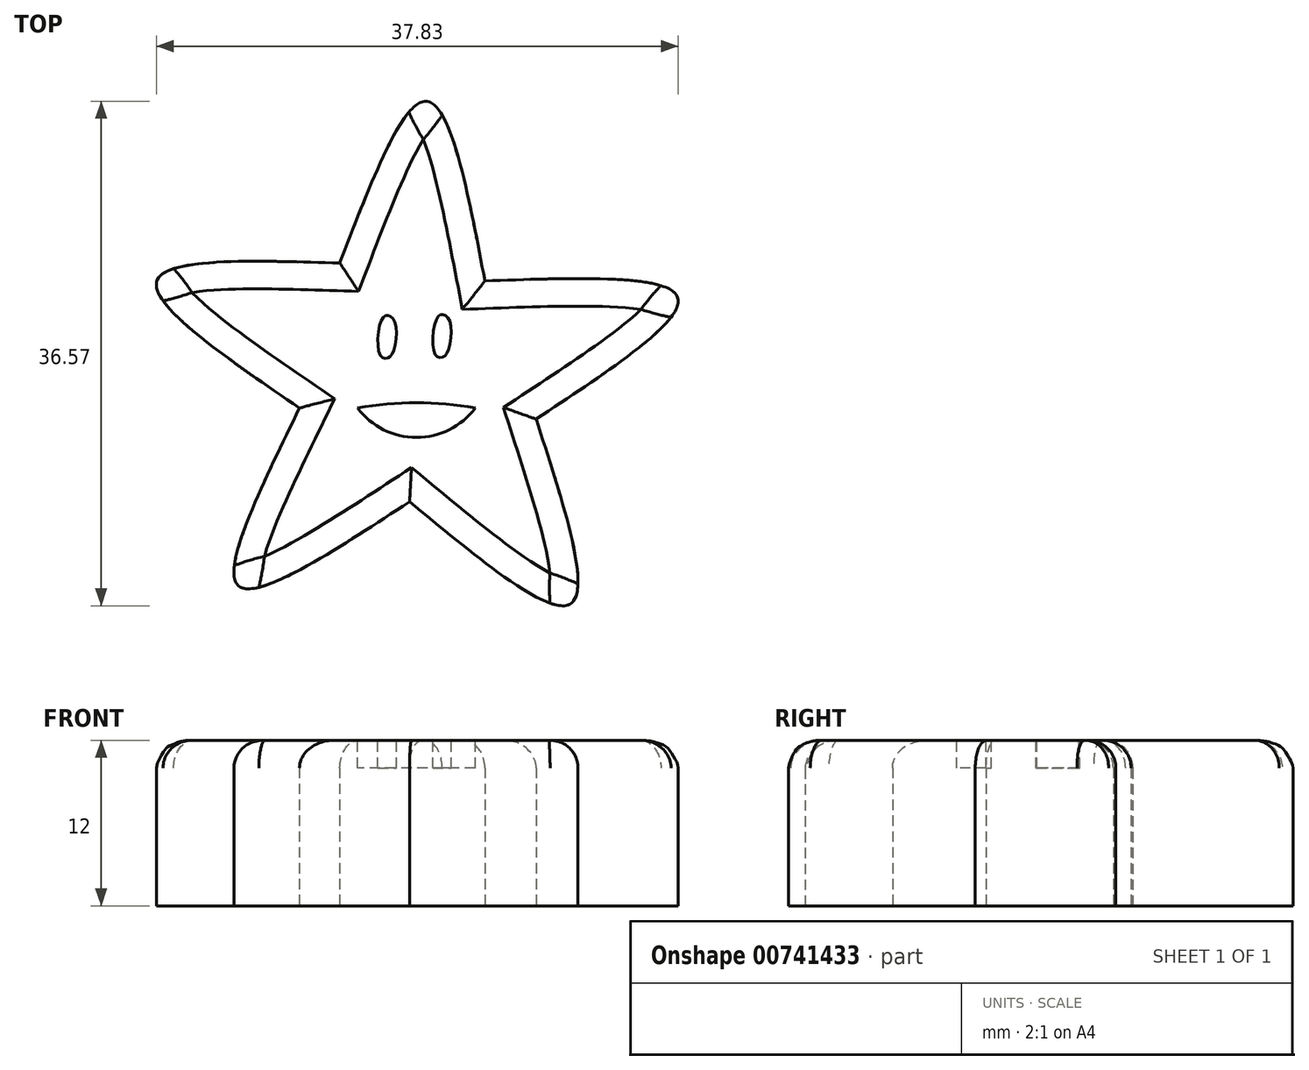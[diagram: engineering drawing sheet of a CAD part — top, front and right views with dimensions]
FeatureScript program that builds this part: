
annotation { "Feature Type Name" : "Feature", "Feature Type Description" : "" }
export const myFeature = defineFeature(function(context is Context, id is Id, definition is map)
    precondition{}
    {
        {
            var Q0;
            Q0=qCreatedBy(makeId("Top.planeOp"),FACE);
            var sketch = newSketch(context, id + "F0", { "sketchPlane" : qUnion([Q0])});
            skLineSegment(sketch, "E0.bottom", {"start": v(25, -20.84) * mm, "end": v(-25, -20.84) * mm});
            skLineSegment(sketch, "E0.top", {"start": v(25, 29.16) * mm, "end": v(-25, 29.16) * mm});
            skLineSegment(sketch, "E0.left", {"start": v(25, -20.84) * mm, "end": v(25, 29.16) * mm});
            skLineSegment(sketch, "E0.right", {"start": v(-25, -20.84) * mm, "end": v(-25, 29.16) * mm});
            skPoint(sketch, "E0.middle", {"position": v(0, 4.16) * mm});
            skSolve(sketch);
        }
        {
            var Q0;
            Q0=qCreatedBy(makeId("Top.planeOp"),FACE);
            var sketch = newSketch(context, id + "F1", { "sketchPlane" : qUnion([Q0])});
            skFitSpline(sketch, "E1", {"points": [v(-5.06, 10.5) * mm, v(1.24, 22.23) * mm, v(5.46, 9.21) * mm], "startDerivative": vector(13.75, 35.91) * mm, "endDerivative": vector(7.31, -38.33) * mm});
            skFitSpline(sketch, "E2", {"points": [v(5.46, 9.21) * mm, v(19.44, 8) * mm, v(9.17, -0.8) * mm], "startDerivative": vector(39.9, 1.48) * mm, "endDerivative": vector(-32.7, -21.56) * mm});
            skFitSpline(sketch, "E3", {"points": [v(9.17, -0.8) * mm, v(11.68, -14.18) * mm, v(0, -6.8) * mm], "startDerivative": vector(12.08, -37.22) * mm, "endDerivative": vector(-30.37, 25.15) * mm});
            skFitSpline(sketch, "E4", {"points": [v(-5.06, 10.5) * mm, v(-18.32, 9.21) * mm, v(-7.98, 0) * mm], "startDerivative": vector(-38.48, 1.26) * mm, "endDerivative": vector(32.4, -22.2) * mm});
            skFitSpline(sketch, "E5", {"points": [v(-7.98, 0) * mm, v(-12.41, -12.88) * mm, v(0, -6.8) * mm], "startDerivative": vector(-17.27, -35.33) * mm, "endDerivative": vector(33.18, 21.68) * mm});
            skSolve(sketch);
        }
        {
            var Q0;
            Q0=qSketchRegion(id+"F1",true);
            extrude(context, id + "F2", {"entities" : qUnion([Q0]), "depth" : 12 * mm, "offsetDistance" : 25 * mm});
        }
        {
            var Q0;
            Q0=makeQuery(id+"F2.opExtrude","CAP_EDGE",EDGE,{"disambiguationData":[OSD([sQuery(id+"F1.wireOp",EDGE,"E4")])],"isStart":false});
            var Q1;
            Q1=makeQuery(id+"F2.opExtrude","CAP_EDGE",EDGE,{"disambiguationData":[OSD([sQuery(id+"F1.wireOp",EDGE,"E5")])],"isStart":false});
            var Q2;
            Q2=makeQuery(id+"F2.opExtrude","CAP_EDGE",EDGE,{"disambiguationData":[OSD([sQuery(id+"F1.wireOp",EDGE,"E3")])],"isStart":false});
            var Q3;
            Q3=makeQuery(id+"F2.opExtrude","CAP_EDGE",EDGE,{"disambiguationData":[OSD([sQuery(id+"F1.wireOp",EDGE,"E2")])],"isStart":false});
            var Q4;
            Q4=makeQuery(id+"F2.opExtrude","CAP_EDGE",EDGE,{"disambiguationData":[OSD([sQuery(id+"F1.wireOp",EDGE,"E1")])],"isStart":false});
            fillet(context, id + "F3", {"entities" : qUnion([Q0, Q1, Q2, Q3, Q4]), "radius" : 2 * mm, "tangentPropagation" : true, "allowEdgeOverflow" : false});
        }
        {
            var Q0;
            Q0=makeQuery(id+"F2.opExtrude","CAP_FACE",FACE,{"disambiguationData":[OSD([sQuery(id+"F1.wireOp",EDGE,"ea22f027-b894-4d35-ad94-6574a105fb3a"),sQuery(id+"F1.wireOp",EDGE,"02972ecb-89ef-400d-9b9c-b38da18b9f26"),sQuery(id+"F1.wireOp",EDGE,"d4665c4b-3644-410e-b7a9-793b46f9e3d8"),sQuery(id+"F1.wireOp",EDGE,"4904a858-6bfa-4176-8c43-c28e2eb22261"),sQuery(id+"F1.wireOp",EDGE,"281288f6-0dfc-4ab6-aa52-0887e6a29920"),sQuery(id+"F1.wireOp",EDGE,"e6a59349-29be-4dfa-85ae-5f5bb5e19001"),sQuery(id+"F1.wireOp",EDGE,"33865bf9-fee0-4887-a290-a33334908563"),sQuery(id+"F1.wireOp",EDGE,"b5a1ea3e-0a3a-46d1-a9d2-b11f3d4d393f"),sQuery(id+"F1.wireOp",EDGE,"9160b71b-1dbf-454e-b8aa-38d11ad0787a"),sQuery(id+"F1.wireOp",EDGE,"508b1097-dadd-43a8-a367-845bdcffccfe"),sQuery(id+"F1.wireOp",EDGE,"49bc861f-a654-40ca-8a3d-e641ddbf638b"),sQuery(id+"F1.wireOp",EDGE,"b91fa5d4-4bf4-43ae-99f3-f47139d4a982"),sQuery(id+"F1.wireOp",EDGE,"91c30a01-8c2e-4a9e-bc94-6af126d221bb"),sQuery(id+"F1.wireOp",EDGE,"46226220-93ab-4b08-822d-1d4fcd13f7f0"),sQuery(id+"F1.wireOp",EDGE,"3cccdf76-d96c-4aba-a423-c60eeaef6f2e"),sQuery(id+"F1.wireOp",EDGE,"a7a83c28-3530-49f8-9c53-c2483f9e7872"),sQuery(id+"F1.wireOp",EDGE,"bd418752-b331-4a27-85c2-437b8f3f9da8"),sQuery(id+"F1.wireOp",EDGE,"d86c6e9c-a8e8-46bc-9cbd-8a8ccbf43cd8"),sQuery(id+"F1.wireOp",EDGE,"18ce2d2a-cbe7-4d55-9af2-434ca90d4d8a"),sQuery(id+"F1.wireOp",EDGE,"3e9cf44d-97a5-4047-a5a6-f93e2a769566"),sQuery(id+"F1.wireOp",EDGE,"72104b77-425f-43ce-bfee-662c898d3039"),sQuery(id+"F1.wireOp",EDGE,"b0c94266-c951-4a47-ba1d-05842cc99b57"),sQuery(id+"F1.wireOp",EDGE,"a3bab185-7591-47d8-8c31-848ac42d466f"),sQuery(id+"F1.wireOp",EDGE,"95482d24-3030-4f51-9019-3cd7c5544abc"),sQuery(id+"F1.wireOp",EDGE,"ecb43bb9-7518-4037-82ed-3b3d48b88220"),sQuery(id+"F1.wireOp",EDGE,"6709acc4-015e-4cee-b4b1-e8162d60af49"),sQuery(id+"F1.wireOp",EDGE,"9c087dd5-8d5f-4c13-9bc7-0dec2b4ae27f"),sQuery(id+"F1.wireOp",EDGE,"1f7cd400-eb1a-477a-a8e0-1a1905c8875b"),sQuery(id+"F1.wireOp",EDGE,"2f4714a1-4b7a-4e27-a0f3-d2b64ee53851"),sQuery(id+"F1.wireOp",EDGE,"cf6d8417-590a-48c5-99af-b32b253a895c"),sQuery(id+"F1.wireOp",EDGE,"93dc3e3c-f9e4-4bb0-b6ea-1e3b1bb8eda1"),sQuery(id+"F1.wireOp",EDGE,"f410118d-9d75-4c7b-a8da-20c13fada343"),sQuery(id+"F1.wireOp",EDGE,"eae4d265-d466-4ba0-ad54-7133bb8090aa"),sQuery(id+"F1.wireOp",EDGE,"29f3a1ae-a44a-4252-90b8-49e4f717a763"),sQuery(id+"F1.wireOp",EDGE,"d95e87fc-c752-4cd3-ba2f-4e1b622d11e6"),sQuery(id+"F1.wireOp",EDGE,"42a256c7-bd9f-4b82-a40e-3aa7b43a7311"),sQuery(id+"F1.wireOp",EDGE,"5cccd7cb-d227-495f-bd2e-dd321fa3711f"),sQuery(id+"F1.wireOp",EDGE,"4779d78b-67a4-4074-8e1d-094c3c882748"),sQuery(id+"F1.wireOp",EDGE,"d78c889f-446d-499c-940c-2d769212d2d6"),sQuery(id+"F1.wireOp",EDGE,"5978d452-f883-4c3a-89cf-e77a3d4812d3"),sQuery(id+"F1.wireOp",EDGE,"d596c75f-4af1-4a7b-b4a9-307fc33695f2"),sQuery(id+"F1.wireOp",EDGE,"ac6da6d2-c422-4b3f-ab3b-024f16e2174f"),sQuery(id+"F1.wireOp",EDGE,"f701fbac-f9f2-41ce-b398-1cdb972a07c6"),sQuery(id+"F1.wireOp",EDGE,"6ea0370e-b9df-47c8-82b6-4bf531107383"),sQuery(id+"F1.wireOp",EDGE,"93d4d691-acf9-4093-813e-c243a6abfd77"),sQuery(id+"F1.wireOp",EDGE,"564c231c-7281-4956-8916-2b9847646294"),sQuery(id+"F1.wireOp",EDGE,"447afba2-fe07-4bf1-a098-a2fa503544db"),sQuery(id+"F1.wireOp",EDGE,"783018d8-4da7-439e-baff-4ea1af6aeaae"),sQuery(id+"F1.wireOp",EDGE,"23360fc8-9112-4eab-be8c-d36215a4c504"),sQuery(id+"F1.wireOp",EDGE,"f39823fe-76bf-4b28-8de3-5866c156ca6e"),sQuery(id+"F1.wireOp",EDGE,"94261188-8fe8-4fe3-9cfb-41c0c768c078"),sQuery(id+"F1.wireOp",EDGE,"639eefb3-3c81-4241-8da9-6294a00eecad"),sQuery(id+"F1.wireOp",EDGE,"63a26b51-3e8c-4d7f-a8c5-c852ed6635fd"),sQuery(id+"F1.wireOp",EDGE,"0cbcce5a-d863-44dc-85fc-889f0cb27286"),sQuery(id+"F1.wireOp",EDGE,"41481716-7baf-47e6-bab9-346e36ad7ed7"),sQuery(id+"F1.wireOp",EDGE,"a0ece215-4608-46fb-b9de-0966884f3722"),sQuery(id+"F1.wireOp",EDGE,"cea85d6a-f16e-43e1-82ab-1eb20eedc667"),sQuery(id+"F1.wireOp",EDGE,"90b3652e-c92f-4129-b232-5fc3862136ad"),sQuery(id+"F1.wireOp",EDGE,"d85ff010-6106-4afe-aa78-55669356d399"),sQuery(id+"F1.wireOp",EDGE,"7b3810e8-a3aa-46c5-9845-10c95717e511"),sQuery(id+"F1.wireOp",EDGE,"32d08b1a-e728-49a8-914d-c4ecc0554df0"),sQuery(id+"F1.wireOp",EDGE,"a932f2cb-edb6-4d43-8a31-36080f450e31"),sQuery(id+"F1.wireOp",EDGE,"6d77b220-5459-4ded-ba71-0805bf8e97fe"),sQuery(id+"F1.wireOp",EDGE,"d4a3d79f-eb9b-45d3-af4d-7f6e0c1d0b6a"),sQuery(id+"F1.wireOp",EDGE,"3a8167d0-93d4-4fee-93fc-e765f78cc71a"),sQuery(id+"F1.wireOp",EDGE,"275b4ef8-3749-467f-b8de-4c5ca6efd012"),sQuery(id+"F1.wireOp",EDGE,"250f3aee-73fb-4a09-89d3-a25958f34bab"),sQuery(id+"F1.wireOp",EDGE,"6f7494f2-175a-490b-9ca9-9ab7524c1492"),sQuery(id+"F1.wireOp",EDGE,"d4bde236-d2fc-4dbc-ba9a-6cd55d3f6a15"),sQuery(id+"F1.wireOp",EDGE,"989c9d0c-4ceb-449c-bc73-c96cc92b2f1a"),sQuery(id+"F1.wireOp",EDGE,"78fda69b-8c10-4e3c-872b-102a69ddef83"),sQuery(id+"F1.wireOp",EDGE,"a15857fb-2d82-4afa-8e36-ecf18161f336"),sQuery(id+"F1.wireOp",EDGE,"b5dc66a1-7abf-40bc-8f4a-394b90f8d275"),sQuery(id+"F1.wireOp",EDGE,"03030db5-3b63-482b-9307-c4991d58ca64"),sQuery(id+"F1.wireOp",EDGE,"17e9b168-3d8f-465c-93a2-82195902c407"),sQuery(id+"F1.wireOp",EDGE,"7465df75-a5ab-45e8-a90a-397120fadcc2"),sQuery(id+"F1.wireOp",EDGE,"16613f2c-828e-433e-977f-464dc0bab4c5"),sQuery(id+"F1.wireOp",EDGE,"47fe3ba8-9260-47cb-bf79-68fdcf4e78a0"),sQuery(id+"F1.wireOp",EDGE,"43b05b75-3a74-4bef-b5f9-64ce1e4d3f92"),sQuery(id+"F1.wireOp",EDGE,"991257b0-d842-40bd-a016-b0dcd5567a51"),sQuery(id+"F1.wireOp",EDGE,"bb4ff494-dc7b-4f0b-a60d-949d5af28021"),sQuery(id+"F1.wireOp",EDGE,"be03492f-4681-4838-bb13-d5d06ba2e1d7"),sQuery(id+"F1.wireOp",EDGE,"97411946-2583-4f17-b8cd-8f9e6a677e8b"),sQuery(id+"F1.wireOp",EDGE,"e440f547-cbda-46c2-b9d7-514191ae65e8"),sQuery(id+"F1.wireOp",EDGE,"60f7c09c-a596-4b98-aa55-1e6369aacef9"),sQuery(id+"F1.wireOp",EDGE,"234aff2d-32ac-438c-92f5-d0bf77c84f1a"),sQuery(id+"F1.wireOp",EDGE,"b87faba7-c0e6-491b-a4a2-d00cc7015cd8"),sQuery(id+"F1.wireOp",EDGE,"90d1a113-3cec-4f00-adab-2e55525ea2b2"),sQuery(id+"F1.wireOp",EDGE,"979cd316-eb47-42a9-a592-d31acdb67cec"),sQuery(id+"F1.wireOp",EDGE,"7428ea2a-103f-4ebb-b4b8-c831fed82aef"),sQuery(id+"F1.wireOp",EDGE,"52370307-3d29-4edd-afa2-faff63602114"),sQuery(id+"F1.wireOp",EDGE,"88128a0f-d6ec-4b0a-bc8b-e0f4bc7cf75c"),sQuery(id+"F1.wireOp",EDGE,"7de87fd6-0158-4915-807c-9afae7a70aa2"),sQuery(id+"F1.wireOp",EDGE,"180d38d7-08b5-478e-9bbb-86c7c12d8af8"),sQuery(id+"F1.wireOp",EDGE,"22979340-1db9-4cf8-9821-84e582c46be2"),sQuery(id+"F1.wireOp",EDGE,"2aecfa87-5c26-43c7-b01b-42edbaea5f26"),sQuery(id+"F1.wireOp",EDGE,"d53a2147-7160-4d9c-aa38-cbb9aa0cbb9e"),sQuery(id+"F1.wireOp",EDGE,"197ff192-98b0-49e9-9c6a-db6e28c6daef"),sQuery(id+"F1.wireOp",EDGE,"ee9a66c0-ba42-4615-a1e3-135759764a0c"),sQuery(id+"F1.wireOp",EDGE,"111631f7-a570-4717-906c-35496458c016"),sQuery(id+"F1.wireOp",EDGE,"bb98202e-b631-4bd4-8df0-c97bad7516e4"),sQuery(id+"F1.wireOp",EDGE,"78248693-6aa8-4cc8-8159-669be31d40dc"),sQuery(id+"F1.wireOp",EDGE,"0797b34a-24f6-40f6-be44-cc817c5cdd3a"),sQuery(id+"F1.wireOp",EDGE,"9025d657-ca05-4ccc-ab26-e4792d65176a"),sQuery(id+"F1.wireOp",EDGE,"3aceb39b-8709-4280-877c-cd3977029748"),sQuery(id+"F1.wireOp",EDGE,"95408ccb-4e7c-4662-8e89-42555b2ea574"),sQuery(id+"F1.wireOp",EDGE,"c1b7ed67-20c2-4104-afb5-83cdaba9b995"),sQuery(id+"F1.wireOp",EDGE,"688e50f1-9262-4d49-9aba-93f33a78428b"),sQuery(id+"F1.wireOp",EDGE,"5589d507-3ac0-4531-9f5c-d9aafc032d42"),sQuery(id+"F1.wireOp",EDGE,"814193a2-ae33-43cb-ab67-dd1ad4c57dc9"),sQuery(id+"F1.wireOp",EDGE,"bd3d597c-a3a3-4bdb-b489-a50847514c41"),sQuery(id+"F1.wireOp",EDGE,"f9c765e2-3d02-412e-b5c8-9cbecb79335e"),sQuery(id+"F1.wireOp",EDGE,"5374216d-eb8c-473a-b232-3210bd6322dc"),sQuery(id+"F1.wireOp",EDGE,"78cd440d-3889-43df-8524-f9ef943d22b7"),sQuery(id+"F1.wireOp",EDGE,"f48db664-ea3d-465f-be7b-7c3f43ebaf76"),sQuery(id+"F1.wireOp",EDGE,"9b5eb5e8-1bde-4125-a0ae-612cc48788f3"),sQuery(id+"F1.wireOp",EDGE,"067b160c-a63e-427f-8b16-299480079f5a"),sQuery(id+"F1.wireOp",EDGE,"672eeee8-6e70-47e9-8364-98da75f5d819"),sQuery(id+"F1.wireOp",EDGE,"5127b20d-0d7c-46bc-be36-6cdcb1b18aaa"),sQuery(id+"F1.wireOp",EDGE,"56f0d7d5-69bd-4014-ad11-0b63b564c3d5"),sQuery(id+"F1.wireOp",EDGE,"9f1370dc-adc3-4c9f-a706-93b7f0c65285"),sQuery(id+"F1.wireOp",EDGE,"4b75f99a-66c5-4a90-8e02-9a1d458dee98"),sQuery(id+"F1.wireOp",EDGE,"d4360ca9-398d-4564-a7bb-61c3d18fbd84"),sQuery(id+"F1.wireOp",EDGE,"57885f1f-bfc3-4972-9dac-58e4406466f0"),sQuery(id+"F1.wireOp",EDGE,"85ac6021-34b8-4ad9-a652-f7b15531d4a2"),sQuery(id+"F1.wireOp",EDGE,"7a21dffe-2b5b-45e4-9271-5292728f147a"),sQuery(id+"F1.wireOp",EDGE,"E1"),sQuery(id+"F1.wireOp",EDGE,"E2"),sQuery(id+"F1.wireOp",EDGE,"E3"),sQuery(id+"F1.wireOp",EDGE,"E4"),sQuery(id+"F1.wireOp",EDGE,"E5")])],"isStart":false});
            var sketch = newSketch(context, id + "F4", { "sketchPlane" : qUnion([Q0])});
            skFitSpline(sketch, "E6", {"points": [v(-1.06, 6.23) * mm, v(-1.6, 6.72) * mm, v(-2.06, 6.33) * mm, v(-2.16, 3.87) * mm, v(-1.66, 3.6) * mm, v(-1.2, 4.07) * mm, v(-1.06, 6.23) * mm]});
            skFitSpline(sketch, "E7", {"points": [v(2.92, 6.29) * mm, v(2.39, 6.79) * mm, v(1.92, 6.39) * mm, v(1.82, 3.93) * mm, v(2.32, 3.67) * mm, v(2.78, 4.13) * mm, v(2.92, 6.29) * mm]});
            skArc(sketch, "E8", {"start": v(-3.77, 0) * mm, "mid": v(0.5, -2.13) * mm, "end": v(4.76, 0) * mm});
            skArc(sketch, "E9", {"start": v(4.76, 0) * mm, "mid": v(0.5, 0.38) * mm, "end": v(-3.77, 0) * mm});
            skArc(sketch, "E10", {"start": v(3.2, -1.39) * mm, "mid": v(0.61, -0.99) * mm, "end": v(-1.95, -1.54) * mm});
            skSolve(sketch);
        }
        {
            var Q0;
            Q0=makeQuery(id+"F4.imprint","IMPRINT",FACE,{"disambiguationData":[TD([[makeQuery(id+"F4.imprint","IMPRINT",EDGE,{"derivedFrom":sQuery(id+"F4.wireOp",EDGE,"E6")}),1.0]])]});
            var Q1;
            Q1=makeQuery(id+"F4.imprint","IMPRINT",FACE,{"disambiguationData":[TD([[makeQuery(id+"F4.imprint","IMPRINT",EDGE,{"derivedFrom":sQuery(id+"F4.wireOp",EDGE,"E7")}),1.0]])]});
            var Q2;
            {var subQ6=sQuery(id+"F4.wireOp",EDGE,"E10");Q2=makeQuery(id+"F4.imprint","IMPRINT",FACE,{"disambiguationData":[TD([[makeQuery(id+"F4.imprint","IMPRINT",EDGE,{"derivedFrom":subQ6}),-1.0]])]});}
            var Q3;
            {var subQ0=sQuery(id+"F4.wireOp",EDGE,"E10");Q3=makeQuery(id+"F4.imprint","IMPRINT",FACE,{"disambiguationData":[TD([[makeQuery(id+"F4.imprint","IMPRINT",EDGE,{"derivedFrom":subQ0}),1.0]])]});}
            var Q4;
            Q4=makeQuery(id+"F4.imprint","IMPRINT",FACE,{"disambiguationData":[TD([[makeQuery(id+"F4.imprint","IMPRINT",EDGE,{"derivedFrom":makeQuery(id+"F2.opExtrude","CAP_EDGE",EDGE,{"disambiguationData":[OSD([sQuery(id+"F1.wireOp",EDGE,"ea22f027-b894-4d35-ad94-6574a105fb3a")])],"isStart":false})}),1.0]])]});
            extrude(context, id + "F5", {"entities" : qUnion([Q0, Q1, Q2, Q3, Q4]), "operationType" : NewBodyOperationType.REMOVE, "oppositeDirection" : true, "depth" : 2 * mm, "offsetDistance" : 25 * mm});
        }
    });
